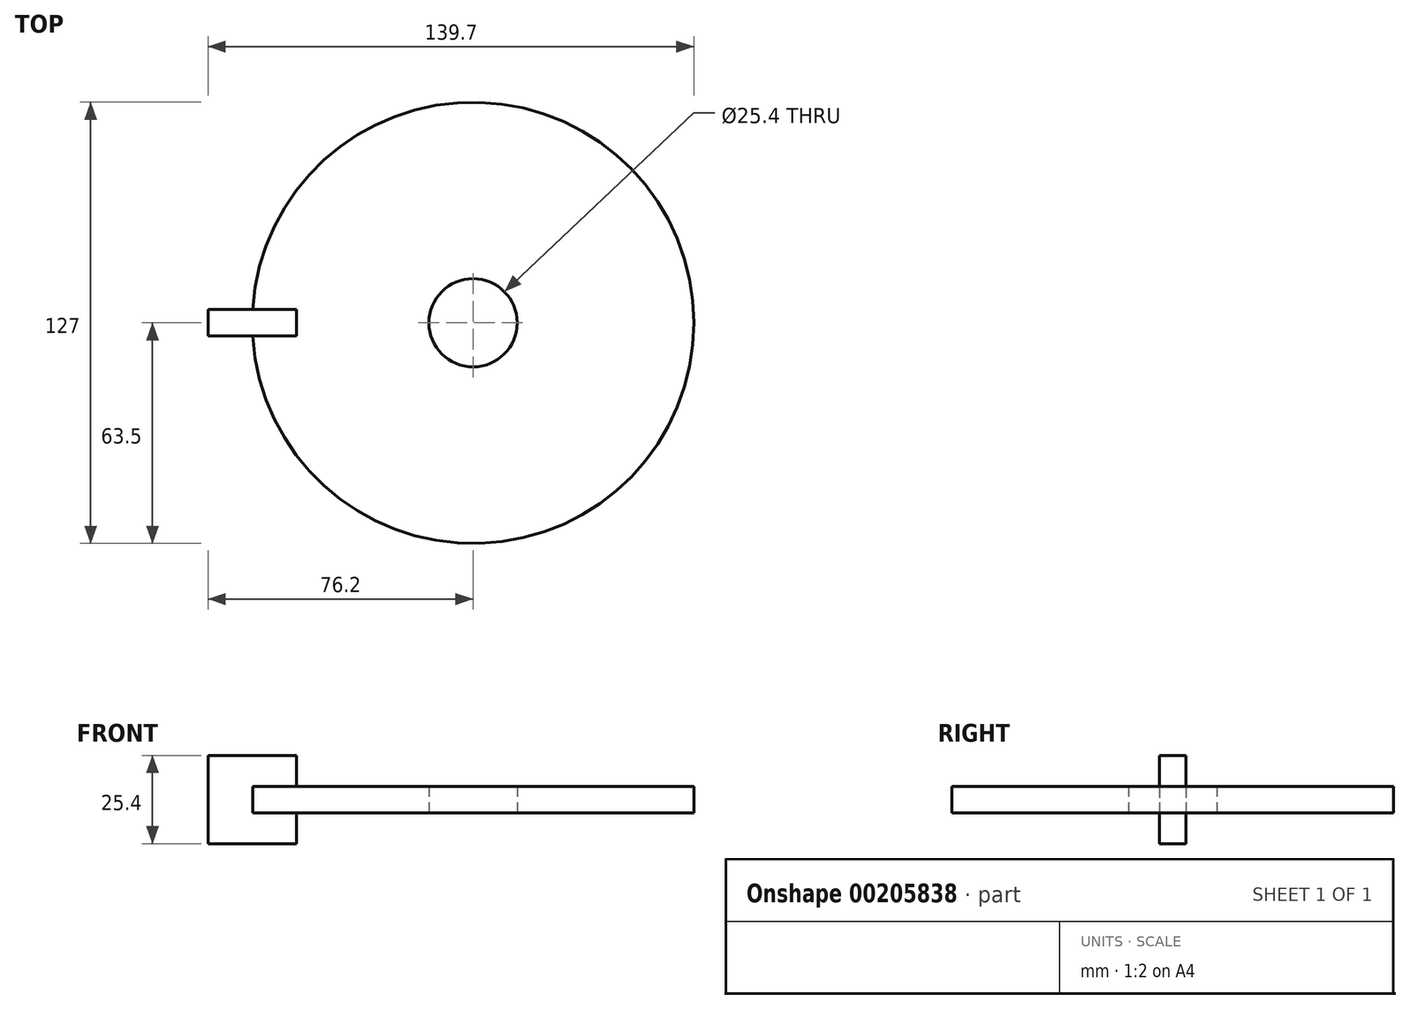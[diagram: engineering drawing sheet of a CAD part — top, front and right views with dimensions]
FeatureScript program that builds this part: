
annotation { "Feature Type Name" : "Feature", "Feature Type Description" : "" }
export const myFeature = defineFeature(function(context is Context, id is Id, definition is map)
    precondition{}
    {
        {
            var Q0;
            Q0=qCreatedBy(makeId("Top.planeOp"),FACE);
            var sketch = newSketch(context, id + "F0", { "sketchPlane" : qUnion([Q0])});
            skCircle(sketch, "E0", {"center": v(0, 0) * mm, "radius": 12.7 * mm});
            skCircle(sketch, "E1", {"center": v(0, 0) * mm, "radius": 63.5 * mm});
            skSolve(sketch);
        }
        {
            var Q0;
            Q0=qCreatedBy(makeId("Top.planeOp"),FACE);
            var sketch = newSketch(context, id + "F1", { "sketchPlane" : qUnion([Q0])});
            skLineSegment(sketch, "E2.bottom", {"start": v(-76.2, 3.81) * mm, "end": v(-50.8, 3.81) * mm});
            skLineSegment(sketch, "E2.top", {"start": v(-76.2, -3.81) * mm, "end": v(-50.8, -3.81) * mm});
            skLineSegment(sketch, "E2.left", {"start": v(-76.2, 3.81) * mm, "end": v(-76.2, -3.81) * mm});
            skLineSegment(sketch, "E2.right", {"start": v(-50.8, 3.81) * mm, "end": v(-50.8, -3.81) * mm});
            skLineSegment(sketch, "E3", {"start": v(-76.2, 0) * mm, "end": v(-50.8, 0) * mm});
            skSolve(sketch);
        }
        {
            var Q0;
            Q0=makeQuery(id+"F0.imprint","IMPRINT",FACE,{"disambiguationData":[TD([[makeQuery(id+"F0.imprint","IMPRINT",EDGE,{"derivedFrom":sQuery(id+"F0.wireOp",EDGE,"E0")}),-1.0]])]});
            extrude(context, id + "F2", {"entities" : qUnion([Q0]), "endBound" : BoundingType.SYMMETRIC, "depth" : 7.62 * mm});
        }
        {
            var Q0;
            Q0 = qSketchRegion(id + "F1", true);
            extrude(context, id + "F3", {"entities" : qUnion([Q0]), "operationType" : NewBodyOperationType.ADD, "endBound" : BoundingType.SYMMETRIC, "depth" : 25.4 * mm});
        }
    });
